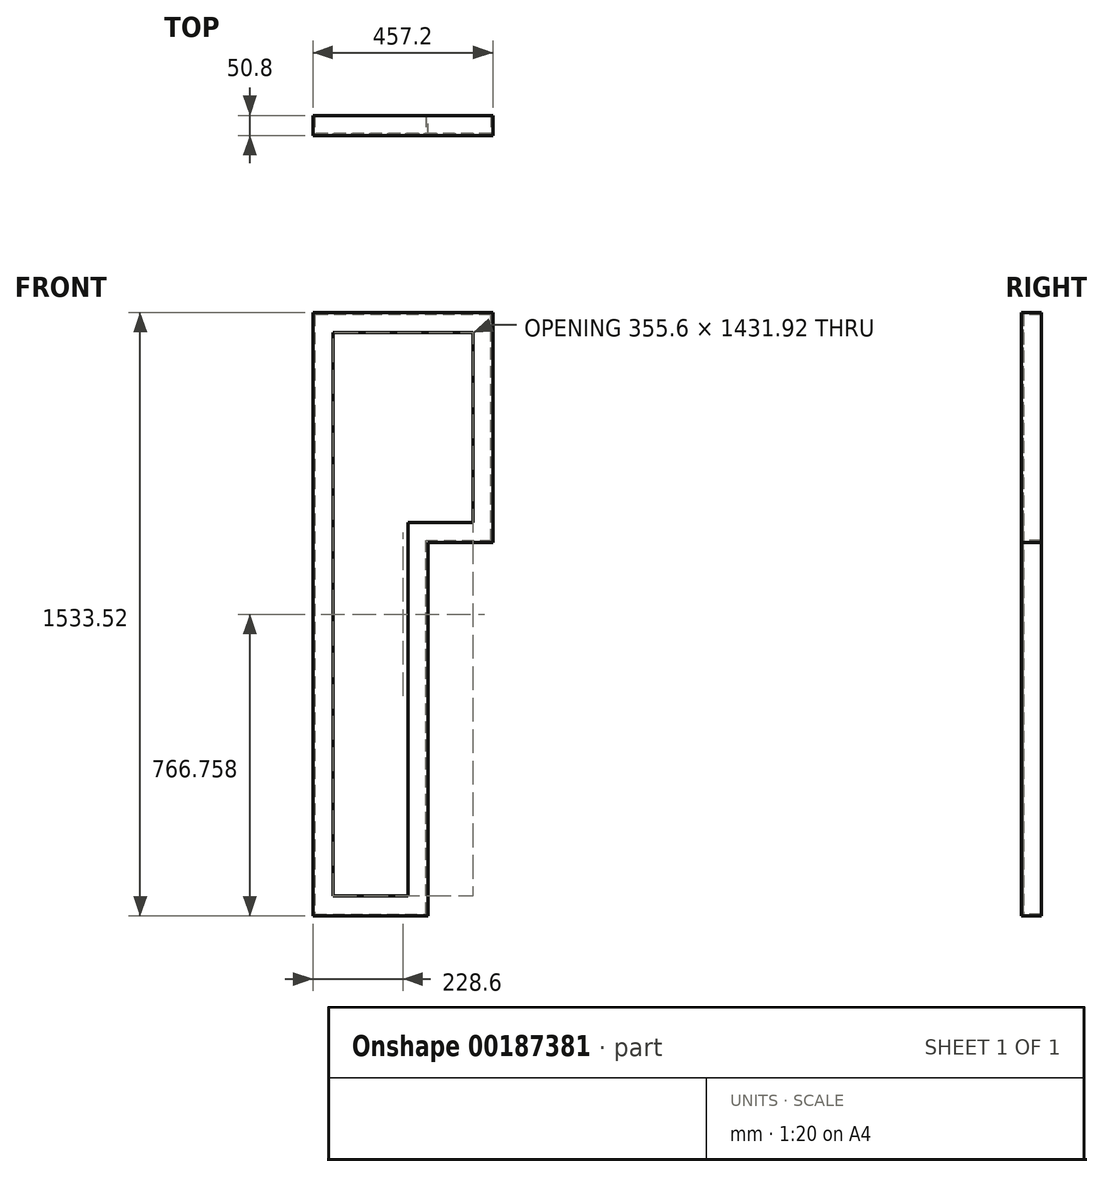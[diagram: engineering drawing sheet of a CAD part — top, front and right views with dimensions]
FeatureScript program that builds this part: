
annotation { "Feature Type Name" : "Feature", "Feature Type Description" : "" }
export const myFeature = defineFeature(function(context is Context, id is Id, definition is map)
    precondition{}
    {
        {
            var Q0;
            Q0=qCreatedBy(makeId("Front.planeOp"),FACE);
            var sketch = newSketch(context, id + "F0", { "sketchPlane" : qUnion([Q0])});
            skLineSegment(sketch, "E0", {"start": v(165.1, 584.2) * mm, "end": v(-292.1, 584.2) * mm});
            skLineSegment(sketch, "E1", {"start": v(-292.1, 584.2) * mm, "end": v(-292.1, -949.33) * mm});
            skLineSegment(sketch, "E2", {"start": v(-292.1, -949.33) * mm, "end": v(0, -949.33) * mm});
            skLineSegment(sketch, "E3", {"start": v(0, -949.32) * mm, "end": v(0, 0) * mm});
            skLineSegment(sketch, "E4", {"start": v(0, 0) * mm, "end": v(165.1, 0) * mm});
            skLineSegment(sketch, "E5", {"start": v(165.1, 0) * mm, "end": v(165.1, 584.2) * mm});
            skLineSegment(sketch, "E6.0", {"start": v(114.3, 533.4) * mm, "end": v(-241.3, 533.4) * mm});
            skLineSegment(sketch, "E6.1", {"start": v(-241.3, -898.53) * mm, "end": v(-50.8, -898.53) * mm});
            skLineSegment(sketch, "E6.2", {"start": v(-50.8, -898.53) * mm, "end": v(-50.8, 50.8) * mm});
            skLineSegment(sketch, "E6.3", {"start": v(-241.3, 533.4) * mm, "end": v(-241.3, -898.53) * mm});
            skLineSegment(sketch, "E6.4", {"start": v(-50.8, 50.8) * mm, "end": v(114.3, 50.8) * mm});
            skLineSegment(sketch, "E6.5", {"start": v(114.3, 50.8) * mm, "end": v(114.3, 533.4) * mm});
            skSolve(sketch);
        }
        {
            var Q0;
            Q0=makeQuery(id+"F0.imprint","IMPRINT",FACE,{"disambiguationData":[TD([[makeQuery(id+"F0.imprint","IMPRINT",EDGE,{"derivedFrom":sQuery(id+"F0.wireOp",EDGE,"E0")}),1.0]])]});
            extrude(context, id + "F1", {"entities" : qUnion([Q0]), "depth" : 4.76 * mm});
        }
        {
            var Q0;
            Q0=makeQuery(id+"F1.opExtrude","CAP_FACE",FACE,{"disambiguationData":[OSD([sQuery(id+"F0.wireOp",EDGE,"E0"),sQuery(id+"F0.wireOp",EDGE,"E1"),sQuery(id+"F0.wireOp",EDGE,"E2"),sQuery(id+"F0.wireOp",EDGE,"E3"),sQuery(id+"F0.wireOp",EDGE,"E4"),sQuery(id+"F0.wireOp",EDGE,"E5"),sQuery(id+"F0.wireOp",EDGE,"E6.0"),sQuery(id+"F0.wireOp",EDGE,"E6.1"),sQuery(id+"F0.wireOp",EDGE,"E6.2"),sQuery(id+"F0.wireOp",EDGE,"E6.3"),sQuery(id+"F0.wireOp",EDGE,"E6.4"),sQuery(id+"F0.wireOp",EDGE,"E6.5")])],"isStart":true});
            var sketch = newSketch(context, id + "F2", { "sketchPlane" : qUnion([Q0])});
            skLineSegment(sketch, "E7.0", {"start": v(4.76, 4.76) * mm, "end": v(-160.34, 4.76) * mm});
            skLineSegment(sketch, "E7.1", {"start": v(-160.34, 579.44) * mm, "end": v(287.34, 579.44) * mm});
            skLineSegment(sketch, "E7.2", {"start": v(287.34, 579.44) * mm, "end": v(287.34, -944.56) * mm});
            skLineSegment(sketch, "E7.3", {"start": v(-160.34, 4.76) * mm, "end": v(-160.34, 579.44) * mm});
            skLineSegment(sketch, "E7.4", {"start": v(287.34, -944.56) * mm, "end": v(4.76, -944.56) * mm});
            skLineSegment(sketch, "E7.5", {"start": v(4.76, -944.56) * mm, "end": v(4.76, 4.76) * mm});
            skSolve(sketch);
        }
        {
            var Q0;
            Q0=makeQuery(id+"F2.imprint","IMPRINT",FACE,{"disambiguationData":[TD([[makeQuery(id+"F2.imprint","IMPRINT",EDGE,{"derivedFrom":sQuery(id+"F2.wireOp",EDGE,"E7.0")}),1.0]])]});
            extrude(context, id + "F3", {"entities" : qUnion([Q0]), "operationType" : NewBodyOperationType.ADD, "depth" : 46.04 * mm});
        }
    });
